# Revit family: Wire_Shelving-Salsbury_Industries-Mobile_Units_48_Wide
name_source: partatom
category: Specialty Equipment
revit_build: Autodesk Revit 2016 (Build: 20150714_1515(x64)
units: mm (PartAtom-declared; Revit-internal decimal feet)

## family parameters
Always vertical = Yes
Cut with Voids When Loaded = No
OmniClass Number = 23.40.00.00
OmniClass Title = Equipment and Furnishings
Part Type = Normal
Room Calculation Point = No
Round Connector Dimension = Use Diameter
Shared = No
Work Plane-Based = No

## types (4) — shared parameters
Assembly Code = C1030320
Assembly Description = Shelving
Manufacturer = Salsbury Industries
MasterFormat Number = 10 56 23
MasterFormat Title = Storage Assemblies
OmniClass 23 Number = 23.40.00.00
OmniClass 23 Title = Equipment and Furnishings
Type Comments = Mobile Wire Shelving
URL = www.lockers.com
Version = 1.0 (07/31/19)
Wheel Hardware = Steel -Salsbury Finish - Polished Steel
Wheel Hub = Plastic - Salsbury Finish - Gray
Wheel Material = Rubber - Salsbury Finish - Black
Width = 48 "

## per-type parameters (varying)
| type | Depth | Description | Height | Shelf 1 | Shelf 2 | Shelf 3 | Shelf 4 |
| 9548M | 18 " | 48" Wide - 69" High - 18" Deep - Certified by the National Sanitation Foundation (NSF) | 69 " | Wire_Shelving-Shelves : 9148 | Wire_Shelving-Shelves : 9148 | Wire_Shelving-Shelves : 9148 | Wire_Shelving-Shelves : 9148 |
| 9544M | 24 " | 48" Wide - 69" High - 24" Deep - Certified by the National Sanitation Foundation (NSF) | 69 " | Wire_Shelving-Shelves : 9144 | Wire_Shelving-Shelves : 9144 | Wire_Shelving-Shelves : 9144 | Wire_Shelving-Shelves : 9144 |
| 9644M | 24 " | 48" Wide - 80" High - 24" Deep - Certified by the National Sanitation Foundation (NSF) | 80 " | Wire_Shelving-Shelves : 9144 | Wire_Shelving-Shelves : 9144 | Wire_Shelving-Shelves : 9144 | Wire_Shelving-Shelves : 9144 |
| 9648M | 18 " | 48" Wide - 80" High - 18" Deep - Certified by the National Sanitation Foundation (NSF) | 80 " | Wire_Shelving-Shelves : 9148 | Wire_Shelving-Shelves : 9148 | Wire_Shelving-Shelves : 9148 | Wire_Shelving-Shelves : 9148 |

note: column(s) folded — value = type name in every type: Model

## geometry (parser evidence)
native form markers: Sweep x17
no freeform markers — native parametric forms only
